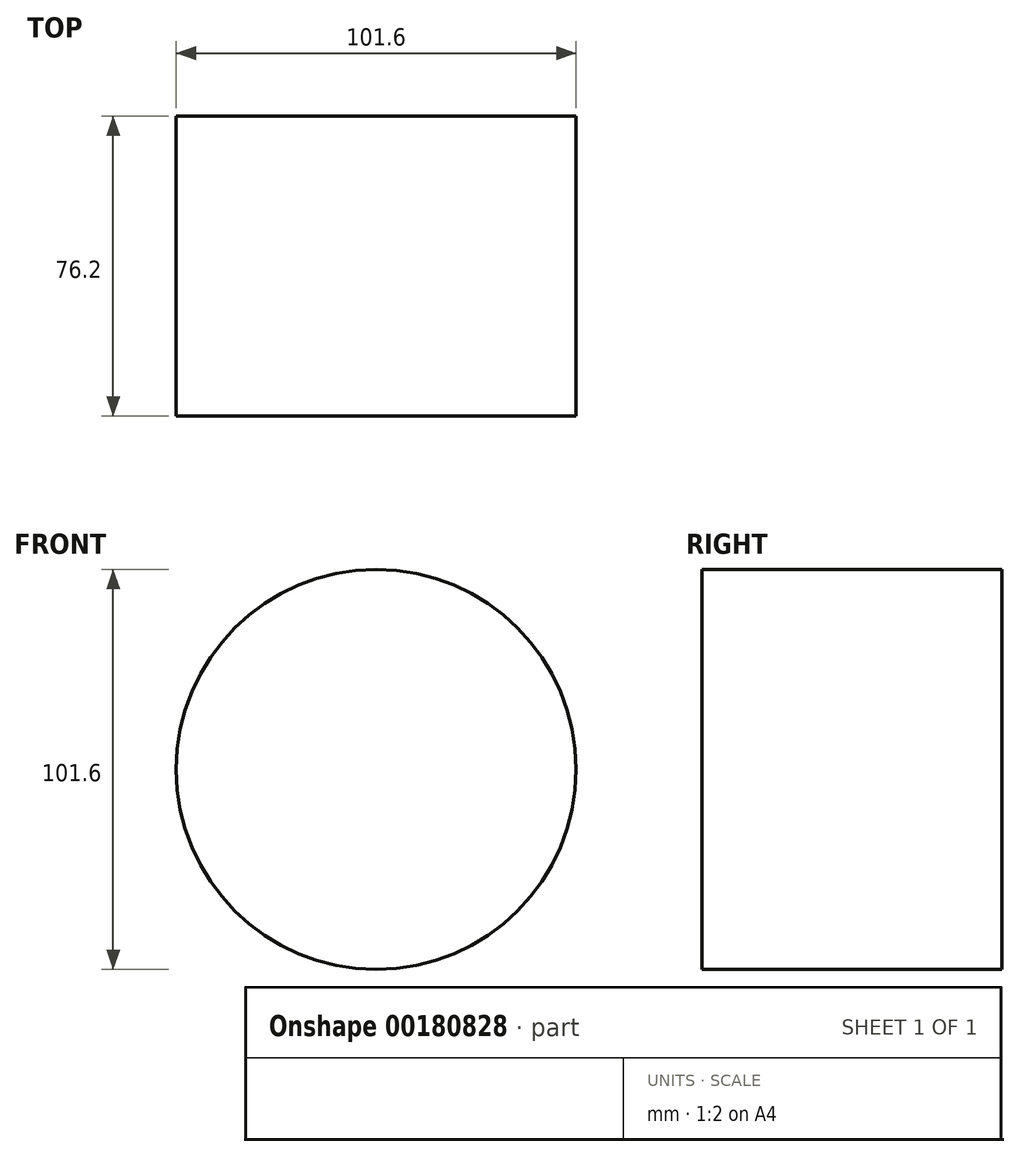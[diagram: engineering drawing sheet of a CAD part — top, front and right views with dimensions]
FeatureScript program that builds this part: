
annotation { "Feature Type Name" : "Feature", "Feature Type Description" : "" }
export const myFeature = defineFeature(function(context is Context, id is Id, definition is map)
    precondition{}
    {
        {
            var Q0;
            Q0=qCreatedBy(makeId("Front.planeOp"),FACE);
            var sketch = newSketch(context, id + "F0", { "sketchPlane" : qUnion([Q0])});
            skCircle(sketch, "E0", {"center": v(0, 0) * mm, "radius": 50.8 * mm});
            skSolve(sketch);
        }
        {
            var Q0;
            Q0 = qSketchRegion(id + "F0", true);
            extrude(context, id + "F1", {"entities" : qUnion([Q0]), "depth" : 76.2 * mm});
        }
    });
